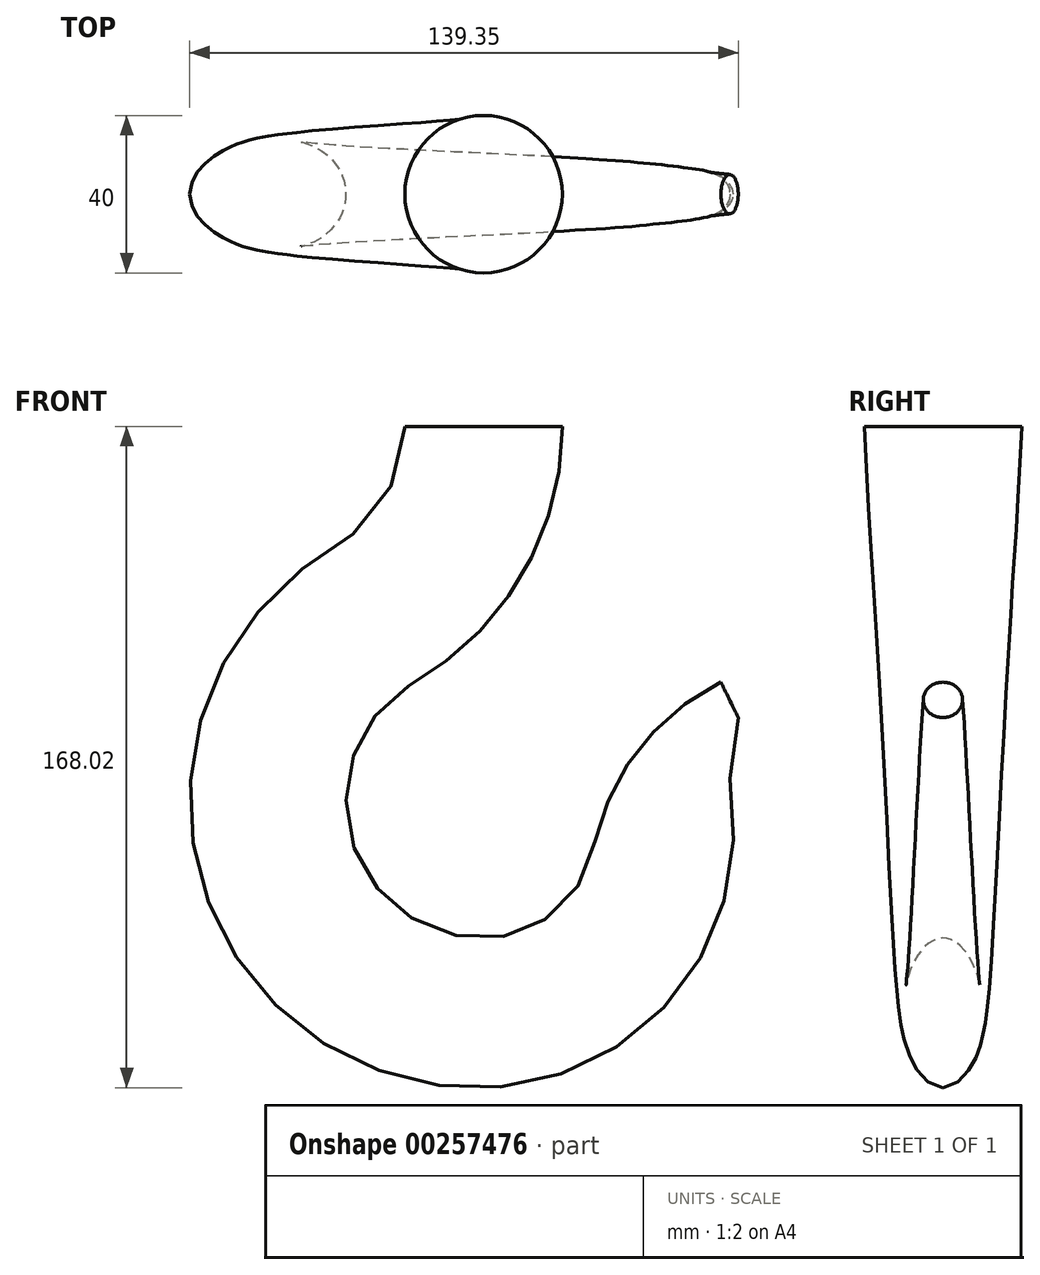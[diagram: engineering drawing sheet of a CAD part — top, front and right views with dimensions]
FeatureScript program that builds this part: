
annotation { "Feature Type Name" : "Feature", "Feature Type Description" : "" }
export const myFeature = defineFeature(function(context is Context, id is Id, definition is map)
    precondition{}
    {
        {
            var Q0;
            Q0=qCreatedBy(makeId("Front.planeOp"),FACE);
            var sketch = newSketch(context, id + "F0", { "sketchPlane" : qUnion([Q0])});
            skLineSegment(sketch, "E0", {"start": v(0, 0) * mm, "end": v(-40, 0) * mm});
            skArc(sketch, "E1", {"start": v(-40, 0) * mm, "mid": v(-44.66, -17.44) * mm, "end": v(-57.39, -30.24) * mm});
            skArc(sketch, "E2", {"start": v(0, 0) * mm, "mid": v(-10.1, -37.58) * mm, "end": v(-37.66, -65.04) * mm});
            skLineSegment(sketch, "E3", {"start": v(-20, 26.41) * mm, "end": v(-20, -249.47) * mm, "construction": true});
            skPoint(sketch, "E3.startSnap0", {"position": v(-20, 0) * mm});
            skLineSegment(sketch, "E4", {"start": v(-212.63, -95) * mm, "end": v(178.63, -95) * mm, "construction": true});
            skPoint(sketch, "E5", {"position": v(-20, -95) * mm});
            skPoint(sketch, "E6", {"position": v(-20, -168) * mm});
            skArc(sketch, "E7", {"start": v(-55, -95) * mm, "mid": v(-44.75, -119.75) * mm, "end": v(-20, -130) * mm});
            skArc(sketch, "E8", {"start": v(-37.66, -65.04) * mm, "mid": v(-50.35, -77.7) * mm, "end": v(-55, -95) * mm});
            skArc(sketch, "E9", {"start": v(-57.39, -30.24) * mm, "mid": v(-84.65, -57.65) * mm, "end": v(-94.64, -95) * mm});
            skArc(sketch, "E10", {"start": v(-94.64, -95) * mm, "mid": v(-72.7, -147.22) * mm, "end": v(-20, -168) * mm});
            skArc(sketch, "E11", {"start": v(-20, -168) * mm, "mid": v(27.79, -145.4) * mm, "end": v(42.98, -94.77) * mm});
            skArc(sketch, "E12", {"start": v(42.98, -94.77) * mm, "mid": v(42.75, -84.28) * mm, "end": v(44.71, -73.97) * mm});
            skLineSegment(sketch, "E13", {"start": v(44.71, -73.97) * mm, "end": v(40.3, -65) * mm});
            skArc(sketch, "E14", {"start": v(40.3, -65) * mm, "mid": v(19.21, -82.27) * mm, "end": v(7.94, -107.09) * mm});
            skArc(sketch, "E15", {"start": v(7.94, -107.09) * mm, "mid": v(-1.93, -123.54) * mm, "end": v(-20, -130) * mm});
            skCircle(sketch, "E16", {"center": v(42.5, -69.49) * mm, "radius": 5 * mm, "construction": true});
            skSolve(sketch);
        }
        {
            var Q0;
            Q0=sQuery(id+"F0.wireOp",EDGE,"E13");
            cPlane(context, id + "F1", {"entities" : qUnion([Q0]), "cplaneType" : CPlaneType.LINE_ANGLE, "offset" : 25 * mm, "angle" : 0 * degree, "width" : 150 * mm, "height" : 150 * mm});
        }
        {
            var Q0;
            Q0=qCreatedBy(id+"F1.planeOp",FACE);
            var sketch = newSketch(context, id + "F2", { "sketchPlane" : qUnion([Q0])});
            skPoint(sketch, "E17.0", {"position": v(0, -76.11) * mm});
            skPoint(sketch, "E18.0", {"position": v(0, -86.11) * mm});
            skPoint(sketch, "E19.0", {"position": v(0, -81.11) * mm});
            skCircle(sketch, "E20", {"center": v(0, -81.11) * mm, "radius": 5 * mm});
            skSolve(sketch);
        }
        {
            var Q0;
            Q0=qCreatedBy(makeId("Top.planeOp"),FACE);
            var sketch = newSketch(context, id + "F3", { "sketchPlane" : qUnion([Q0])});
            skPoint(sketch, "E21.0", {"position": v(-20, 0) * mm});
            skCircle(sketch, "E22", {"center": v(-20, 0) * mm, "radius": 20 * mm});
            skSolve(sketch);
        }
        {
            var Q0;
            Q0=makeQuery(id+"F0.imprint","IMPRINT",FACE,{"disambiguationData":[TD([[makeQuery(id+"F0.imprint","IMPRINT",EDGE,{"derivedFrom":sQuery(id+"F0.wireOp",EDGE,"E0")}),1.0]])]});
            var sketch = newSketch(context, id + "F4", { "sketchPlane" : qUnion([Q0])});
            skArc(sketch, "E23.0", {"start": v(-40, 0) * mm, "mid": v(-44.66, -17.44) * mm, "end": v(-57.39, -30.24) * mm});
            skArc(sketch, "E24.0", {"start": v(-57.39, -30.24) * mm, "mid": v(-84.65, -57.65) * mm, "end": v(-94.64, -95) * mm});
            skArc(sketch, "E25.0", {"start": v(-94.64, -95) * mm, "mid": v(-72.7, -147.22) * mm, "end": v(-20, -168) * mm});
            skArc(sketch, "E26.0", {"start": v(-20, -168) * mm, "mid": v(27.79, -145.4) * mm, "end": v(42.98, -94.77) * mm});
            skArc(sketch, "E27.0", {"start": v(42.98, -94.77) * mm, "mid": v(42.75, -84.28) * mm, "end": v(44.71, -73.97) * mm});
            skSolve(sketch);
        }
        {
            var Q0;
            Q0=makeQuery(id+"F0.imprint","IMPRINT",FACE,{"disambiguationData":[TD([[makeQuery(id+"F0.imprint","IMPRINT",EDGE,{"derivedFrom":sQuery(id+"F0.wireOp",EDGE,"E0")}),1.0]])]});
            var sketch = newSketch(context, id + "F5", { "sketchPlane" : qUnion([Q0])});
            skArc(sketch, "E28.0", {"start": v(0, 0) * mm, "mid": v(-10.1, -37.58) * mm, "end": v(-37.66, -65.04) * mm});
            skArc(sketch, "E29.0", {"start": v(-37.66, -65.04) * mm, "mid": v(-50.35, -77.7) * mm, "end": v(-55, -95) * mm});
            skArc(sketch, "E30.0", {"start": v(-55, -95) * mm, "mid": v(-44.75, -119.75) * mm, "end": v(-20, -130) * mm});
            skArc(sketch, "E31.0", {"start": v(7.94, -107.09) * mm, "mid": v(-1.93, -123.54) * mm, "end": v(-20, -130) * mm});
            skArc(sketch, "E31.1", {"start": v(40.3, -65) * mm, "mid": v(19.21, -82.27) * mm, "end": v(7.94, -107.09) * mm});
            skSolve(sketch);
        }
        {
            var Q0;
            Q0=makeQuery(id+"F3.imprint","IMPRINT",FACE,{"disambiguationData":[TD([[makeQuery(id+"F3.imprint","IMPRINT",EDGE,{"derivedFrom":sQuery(id+"F3.wireOp",EDGE,"E22")}),1.0]])]});
            var Q1;
            Q1=makeQuery(id+"F2.imprint","IMPRINT",FACE,{"disambiguationData":[TD([[makeQuery(id+"F2.imprint","IMPRINT",EDGE,{"derivedFrom":sQuery(id+"F2.wireOp",EDGE,"E20")}),1.0]])]});
            var Q2;
            Q2 = qConstructionFilter(qBodyType(qCreatedBy(id + "F4" ,EDGE), BodyType.WIRE), ConstructionObject.NO);
            var Q3;
            Q3 = qConstructionFilter(qBodyType(qCreatedBy(id + "F5" ,EDGE), BodyType.WIRE), ConstructionObject.NO);
            loft(context, id + "F6", {"addGuides" : true, "sheetProfilesArray" : [{ "sheetProfileEntities" : qUnion([Q0]) }, { "sheetProfileEntities" : qUnion([Q1]) }], "guidesArray" : [{ "guideEntities" : qUnion([Q2]), "guideDerivativeType" : LoftGuideDerivativeType.DEFAULT, "guideDerivativeMagnitude" : 1 }, { "guideEntities" : qUnion([Q3]), "guideDerivativeType" : LoftGuideDerivativeType.DEFAULT, "guideDerivativeMagnitude" : 1 }]});
        }
    });
